# Revit family: IS_Septa_R0131_BIM_DE
name_source: partatom
category: Plumbing Fixtures
revit_build: Autodesk Revit 2017 (Build: 20160225_1515(x64)
units: mm (PartAtom-declared; Revit-internal decimal feet)

## family parameters
Always vertical = Yes
Cut with Voids When Loaded = No
OmniClass Number = 23.45.00.00
OmniClass Title = Sanitary, Laundry, and Cleaning Equipment
Part Type = Normal
Room Calculation Point = No
Round Connector Dimension = Use Diameter
Shared = No
Work Plane-Based = Yes

## types (1)
- R0131AA - SEPTA PRO E1 CHROME - IS
    Afmetingen = 0
    AfstandsEenheid = millimeters
    Afwerking = 0
    Artikelnummer = R0131AA
    Artikelomschrijving = Betätigungsplatte M3 OLEAS, mechanischen Auslösung, Schwarz
    Artikelreferentie = 1
    Auteur = Ideal Standrad
    Barcode = 0
    Beschrijvinggarantie = Manufacturers Warranty
    BimObjectNaam = 0
    Breedte = 0
    BrutoGewicht = 0
    CONTROL_Brief description = High-tech inside and out. Electronic control plate with infrared sensor and mechanical atuation
    CONTROL_Height = 163 mm  [stored 0.534777 ft]
    CONTROL_Length = 243 mm
    CONTROL_Material = Polished chrome Zamac
    CONTROL_Width = 14 mm  [stored 0.0459318 ft]
    Default Elevation = 900 mm  [stored 2.95276 ft]
    Description = AntiVandal Proximity plate, CP DF including mechanical actuation
    Diepte = 0 mm  [stored 0 ft]
    Douchebak = No
    DuurEenheid = year
    Garantieunits = Year
    GrootteAfvoergat = 0
    Heefthandvaten = No
    Hulp = https://www.idealstandard.de
    Installatieinstructies = https://www.idealstandard.de
    Kleur = 0
    Lengte = 0 mm  [stored 0 ft]
    Materiaal = Metal
    Merk = Ideal Standard
    Model = R0131AA
    Montageinstuctie = https://www.idealstandard.de
    Nettogewicht = 0.9
    Overloop = 0 mm  [stored 0 ft]
    Productinformatie = https://www.idealstandard.de
    Telefoonnummer = +49 (0) 6571 16 0
    URL = https://www.idealstandard.de
    Uniclass2015Referentie = Pr_40_20_93
    Urlproducent = https://www.idealstandard.de
    Versie = 1
    Vervangingskosten = 0
    Verwachtelevensduur = 5
    Volumeunits = Litres

note: [stored X ft] marks values corroborated as IEEE doubles in the binary element streams (Revit-internal decimal feet)

## geometry (parser evidence)
native form markers: Sweep x4
no freeform markers — native parametric forms only
